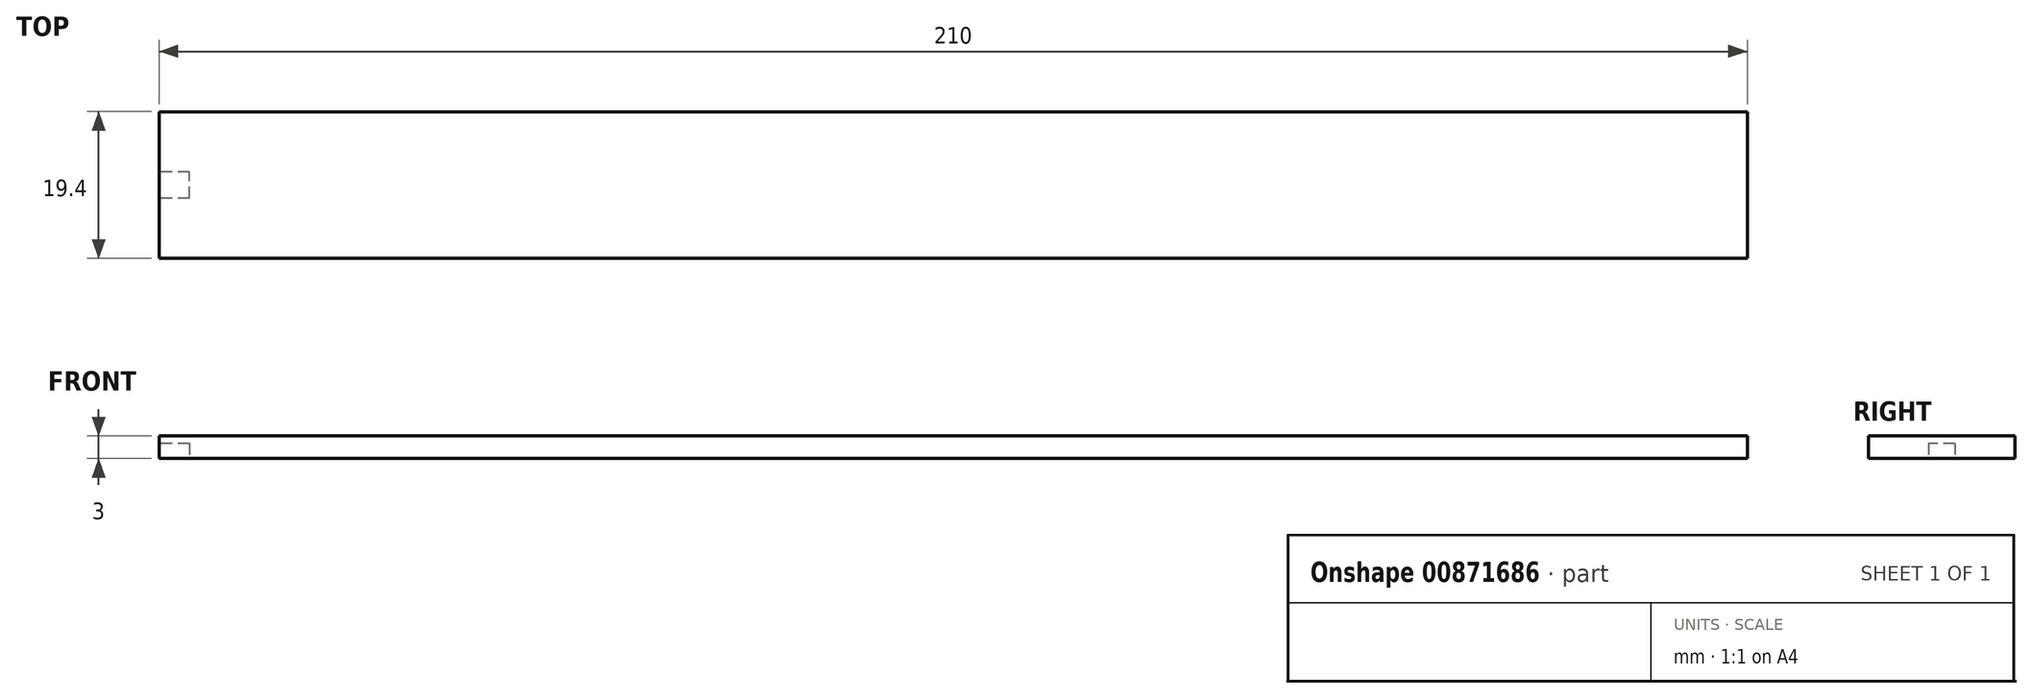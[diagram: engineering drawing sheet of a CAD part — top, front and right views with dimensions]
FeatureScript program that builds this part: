
annotation { "Feature Type Name" : "Feature", "Feature Type Description" : "" }
export const myFeature = defineFeature(function(context is Context, id is Id, definition is map)
    precondition{}
    {
        {
            var Q0;
            Q0=qCreatedBy(makeId("Top.planeOp"),FACE);
            var sketch = newSketch(context, id + "F0", { "sketchPlane" : qUnion([Q0])});
            skLineSegment(sketch, "E0.bottom", {"start": v(105, -9.7) * mm, "end": v(-105, -9.7) * mm});
            skLineSegment(sketch, "E0.top", {"start": v(105, 9.7) * mm, "end": v(-105, 9.7) * mm});
            skLineSegment(sketch, "E0.left", {"start": v(105, -9.7) * mm, "end": v(105, 9.7) * mm});
            skLineSegment(sketch, "E0.right", {"start": v(-105, -9.7) * mm, "end": v(-105, 9.7) * mm});
            skPoint(sketch, "E0.middle", {"position": v(0, 0) * mm});
            skSolve(sketch);
        }
        {
            var Q0;
            Q0=qSketchRegion(id+"F0",true);
            extrude(context, id + "F1", {"entities" : qUnion([Q0]), "depth" : 3 * mm, "offsetDistance" : 25 * mm});
        }
        {
            var Q0;
            Q0=makeQuery(id+"F1.opExtrude","SWEPT_FACE",FACE,{"disambiguationData":[OSD([sQuery(id+"F0.wireOp",EDGE,"E0.left")])]});
            var sketch = newSketch(context, id + "F2", { "sketchPlane" : qUnion([Q0])});
            skLineSegment(sketch, "E1.bottom", {"start": v(-1.5, 1.5) * mm, "end": v(1.5, 1.5) * mm});
            skLineSegment(sketch, "E1.top", {"start": v(-1.5, 0) * mm, "end": v(1.5, 0) * mm});
            skLineSegment(sketch, "E1.left", {"start": v(-1.5, 1.5) * mm, "end": v(-1.5, 0) * mm});
            skLineSegment(sketch, "E1.right", {"start": v(1.5, 1.5) * mm, "end": v(1.5, 0) * mm});
            skLineSegment(sketch, "E2", {"start": v(0, 0) * mm, "end": v(0, 1.96) * mm, "construction": true});
            skSolve(sketch);
        }
        {
            var Q0;
            Q0=makeQuery(id+"F1.opExtrude","SWEPT_FACE",FACE,{"disambiguationData":[OSD([sQuery(id+"F0.wireOp",EDGE,"E0.right")])]});
            var sketch = newSketch(context, id + "F3", { "sketchPlane" : qUnion([Q0])});
            skLineSegment(sketch, "E3.bottom", {"start": v(-1.75, 2) * mm, "end": v(1.75, 2) * mm});
            skLineSegment(sketch, "E3.top", {"start": v(-1.75, 0) * mm, "end": v(1.75, 0) * mm});
            skLineSegment(sketch, "E3.left", {"start": v(-1.75, 2) * mm, "end": v(-1.75, 0) * mm});
            skLineSegment(sketch, "E3.right", {"start": v(1.75, 2) * mm, "end": v(1.75, 0) * mm});
            skLineSegment(sketch, "E4", {"start": v(0, 0) * mm, "end": v(0, 3) * mm, "construction": true});
            skSolve(sketch);
        }
        {
            var Q0;
            Q0=qSketchRegion(id+"F3",true);
            extrude(context, id + "F4", {"entities" : qUnion([Q0]), "operationType" : NewBodyOperationType.REMOVE, "oppositeDirection" : true, "depth" : 4 * mm, "offsetDistance" : 25 * mm});
        }
    });
